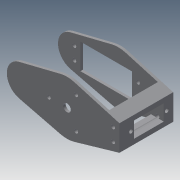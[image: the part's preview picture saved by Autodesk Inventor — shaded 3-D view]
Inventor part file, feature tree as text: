
AUTODESK INVENTOR PART (.ipt)
format: ipt  version: 2013 (Build 170138000, 138)  size: 556,544 bytes
history: native  units: mm
features: sketch x41, extrude x40
ambient origin geometry x8: Origin, YZ Plane, XZ Plane, XY Plane, X Axis, Y Axis, Z Axis, Center Point
bodies: Solid1 (feature_tree)
feature tree (81):
  extrude  "Extrusion1"  Depth=20.0mm
  extrude  "Extrusion2"  Depth=10.0mm
  extrude  "Extrusion3"  Depth=6.0mm
  extrude  "Extrusion4"  Depth=48.0mm TaperAngle=0.0deg
  extrude  "Extrusion5"  Depth=6.0mm
  extrude  "Extrusion6"  Depth=2.05mm
  extrude  "Extrusion7"  Depth=3.0mm
  extrude  "Extrusion8"  Depth=2.35mm
  extrude  "Extrusion9"  Depth=12.4mm
  extrude  "Extrusion10"  Depth=3.0mm
  extrude  "Extrusion11"  TaperAngle=60.0deg  [1 undecoded]
  extrude  "Extrusion12"  Depth=3.0mm
  extrude  "Extrusion13"  Depth=1.0mm TaperAngle=0.0deg
  extrude  "Extrusion14"  Depth=1.0mm TaperAngle=0.0deg
  sketch  "Sketch15"  dims[d46=1.0mm d47=0.0mm d52=3.0mm]
  extrude  "Extrusion15"  Depth=3.0mm
  extrude  "Extrusion16"  Depth=2.0mm TaperAngle=0.0deg
  extrude  "Extrusion17"  Depth=20.0mm
  extrude  "Extrusion18"  Depth=40.2mm
  extrude  "Extrusion19"  Depth=3.0mm
  sketch  "Sketch20"  dims[d72=3.0mm d73=3.0mm]
  extrude  "Extrusion20"  Depth=3.0mm
  extrude  "Extrusion21"  Depth=3.0mm
  extrude  "Extrusion22"  Depth=2.0mm TaperAngle=0.0deg
  extrude  "Extrusion23"  Depth=18.1mm
  extrude  "Extrusion24"  Depth=3.0mm
  extrude  "Extrusion25"  Depth=3.0mm
  extrude  "Extrusion26"  Depth=2.0mm TaperAngle=0.0deg
  extrude  "Extrusion27"  Depth=3.0mm
  extrude  "Extrusion28"  Depth=3.0mm
  extrude  "Extrusion29"  Depth=2.0mm TaperAngle=0.0deg
  extrude  "Extrusion30"  Depth=3.0mm
  extrude  "Extrusion31"  Depth=3.0mm
  extrude  "Extrusion32"  Depth=18.1mm
  extrude  "Extrusion33"  Depth=2.0mm TaperAngle=0.0deg
  extrude  "Extrusion34"  Depth=8.0mm TaperAngle=0.0deg
  extrude  "Extrusion35"  Depth=40.2mm
  extrude  "Extrusion36"  Depth=2.0mm TaperAngle=0.0deg
  extrude  "Extrusion37"  Depth=4.0mm TaperAngle=0.0deg
  extrude  "Extrusion38"  Depth=4.0mm TaperAngle=0.0deg
  extrude  "Extrusion39"  Depth=10.0mm TaperAngle=0.0deg
  extrude  "Extrusion40"  Depth=2.0mm
  sketch  "Sketch1"  dims[d0=42.0mm d1=20.0mm]
  sketch  "Sketch2"  dims[d2=10.0mm d3=10.0mm]
  sketch  "Sketch3"  dims[d9=2.0mm d10=0.0mm d11=6.0mm]
  sketch  "Sketch4"  dims[d12=2.0mm d13=0.0mm d15=48.0mm d16=0.0mm]
  sketch  "Sketch5"  dims[d17=42.0mm d18=6.0mm]
  sketch  "Sketch6"  dims[d19=2.0mm d20=0.0mm d23=2.05mm]
  sketch  "Sketch7"  dims[d24=2.05mm d25=3.0mm]
  sketch  "Sketch8"  dims[d26=3.0mm d27=2.35mm]
  sketch  "Sketch9"  dims[d28=2.35mm d29=12.4mm]
  sketch  "Sketch10"  dims[d30=2.0mm d31=0.0mm d33=3.0mm]
  sketch  "Sketch11"  dims[d34=60.0deg d35=60.0deg]
  sketch  "Sketch12"  dims[d36=3.0mm d37=3.0mm]
  sketch  "Sketch13"  dims[d38=2.0mm d39=0.0mm d40=1.0mm d41=0.0mm]
  sketch  "Sketch14"  dims[d42=1.0mm d43=0.0mm d44=1.0mm d45=0.0mm]
  sketch  "Sketch16"  dims[d53=3.0mm d54=2.0mm d55=0.0mm]
  sketch  "Sketch17"  dims[d58=55.0mm d59=20.0mm]
  sketch  "Sketch18"  dims[d61=10.0mm d62=40.2mm]
  sketch  "Sketch19"  dims[d67=3.0mm d69=3.0mm]
  sketch  "Sketch21"  dims[d74=2.0mm d75=0.0mm d77=3.0mm]
  sketch  "Sketch22"  dims[d79=3.0mm d80=2.0mm d81=0.0mm]
  sketch  "Sketch23"  dims[d83=46.0mm d84=0.0mm d85=18.1mm]
  sketch  "Sketch24"  dims[d87=2.65mm d92=3.0mm]
  sketch  "Sketch25"  dims[d93=3.0mm d95=3.0mm]
  sketch  "Sketch26"  dims[d96=3.0mm d97=2.0mm d98=0.0mm]
  sketch  "Sketch27"  dims[d99=2.0mm d100=0.0mm d101=3.0mm]
  sketch  "Sketch28"  dims[d102=3.0mm d103=3.0mm]
  sketch  "Sketch29"  dims[d104=3.0mm d105=2.0mm d106=0.0mm]
  sketch  "Sketch30"  dims[d108=3.0mm d109=3.0mm]
  sketch  "Sketch31"  dims[d110=2.65mm d112=3.0mm]
  sketch  "Sketch32"  dims[d113=3.0mm d114=18.1mm]
  sketch  "Sketch33"  dims[d115=65.0mm d116=2.0mm d117=0.0mm]
  sketch  "Sketch34"  dims[d118=2.0mm d119=0.0mm d124=8.0mm d125=0.0mm]
  sketch  "Sketch35"  dims[d126=46.0mm d127=0.0mm d131=40.2mm]
  sketch  "Sketch36"  dims[d132=2.0mm d133=0.0mm d134=2.0mm d135=0.0mm]
  sketch  "Sketch37"  dims[d136=2.0mm d137=0.0mm d138=4.0mm d139=0.0mm]
  sketch  "Sketch38"  dims[d140=4.0mm d141=0.0mm d142=4.0mm d143=0.0mm]
  sketch  "Sketch39"  dims[d144=4.0mm d145=0.0mm d146=10.0mm d147=0.0mm]
  sketch  "Sketch40"  dims[d148=10.0mm d149=0.0mm d150=2.0mm]
  sketch  "Sketch41"  dims[d153=2.0mm d161=4.1mm d163=3.0mm d164=3.0mm d165=12.4mm d166=23.2mm d167=10.0mm d168=0.0mm d170=3.0mm d171=3.0mm d172=42.0mm d173=0.0mm d174=2.0mm d175=0.0mm d176=2.0mm d177=0.0mm d178=2.0mm d179=0.0mm d180=40.2mm d183=3.0mm d184=3.0mm d185=2.0mm d186=0.0mm d187=34.25mm d188=2.0mm d189=0.0mm d190=2.0mm d191=0.0mm d192=2.0mm d193=0.0mm d194=2.0mm d195=0.0mm]
note: 1 required parameter value undecoded (feature->parameter linkage not recoverable at this tier; creation-order binding heuristic only, values carry confidence <= 0.55)
